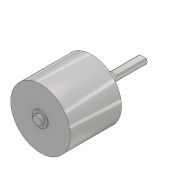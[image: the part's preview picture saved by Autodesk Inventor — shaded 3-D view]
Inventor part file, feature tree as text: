
AUTODESK INVENTOR PART (.ipt)
format: ipt  version: 2018 (Build 220112000, 112)  size: 136,704 bytes
history: native  units: mm
features: extrude x6, sketch x6, fillet x1, projected_geometry x1
ambient origin geometry x8: Origin, YZ Plane, XZ Plane, XY Plane, X Axis, Y Axis, Z Axis, Center Point
bodies: Solid1 (feature_tree)
feature tree (14):
  extrude  "Extrusion1"  Depth=30.0mm TaperAngle=0.0deg
  extrude  "Extrusion2"  Depth=2.0mm TaperAngle=0.0deg
  extrude  "Extrusion3"  Depth=30.0mm TaperAngle=0.0deg
  extrude  "Extrusion5"  Depth=9.0mm
  extrude  "Extrusion6"  Depth=3.0mm
  extrude  "Extrusion7"  Depth=0.5mm TaperAngle=0.0deg
  fillet  "Fillet1"  Radius=1.5mm
  sketch  "Sketch1"  dims[d0=35.0mm d1=30.0mm d2=0.0mm]
  sketch  "Sketch2"  dims[d3=5.0mm d4=2.0mm d5=0.0mm]
  sketch  "Sketch3"  dims[d6=5.0mm d7=30.0mm d8=0.0mm]
  sketch  "Sketch4"  dims[d9=9.0mm d12=5.5mm]
  sketch  "Sketch5"  dims[d13=3.0mm d14=0.0mm d15=5.5mm]
  sketch  "Sketch6"  dims[d16=9.0mm d17=0.5mm d18=0.0mm d19=1.5mm d20=18.0mm d21=0.0mm d22=0.5mm]
  projected_geometry  "Projected Loop1"
